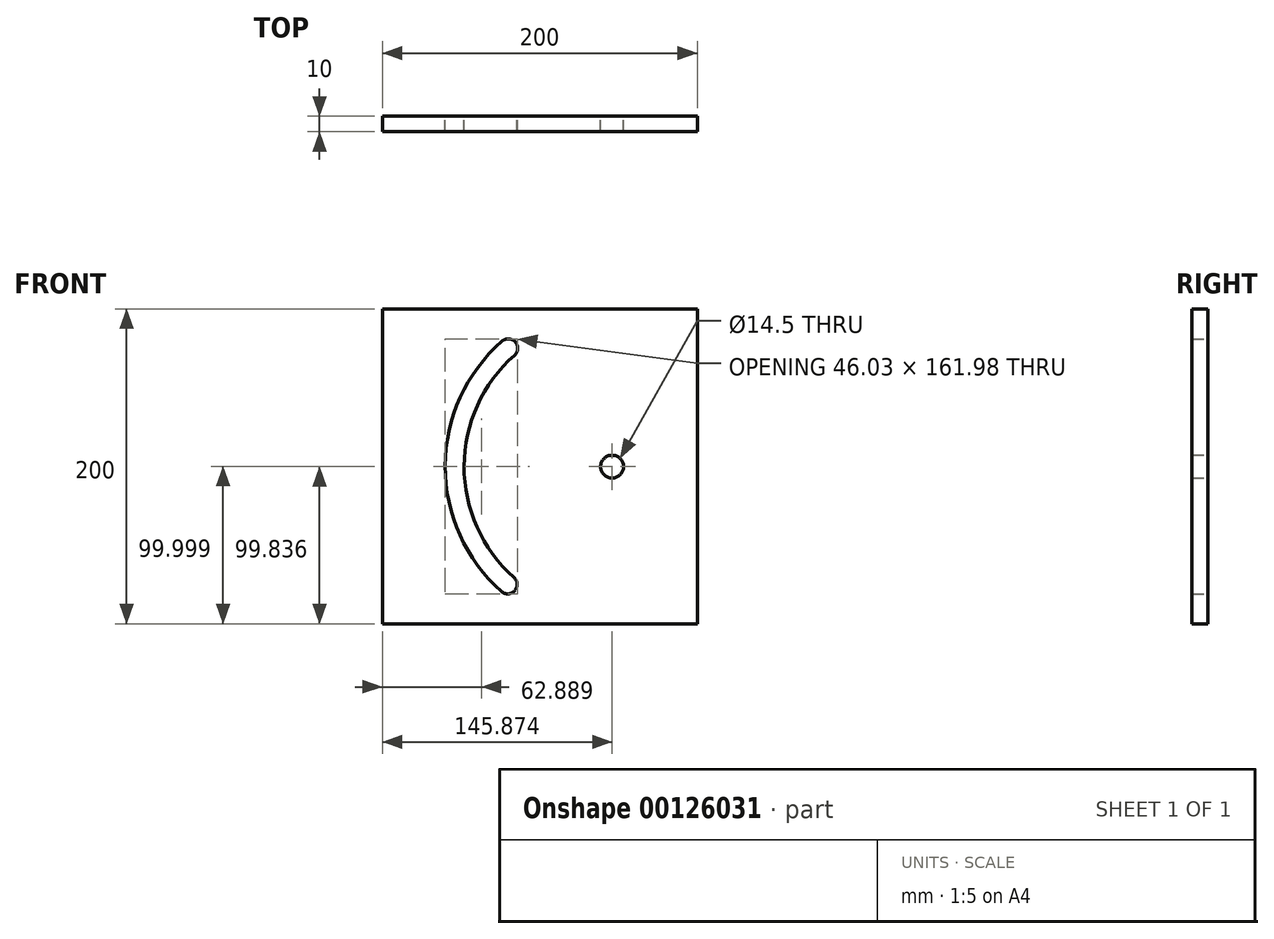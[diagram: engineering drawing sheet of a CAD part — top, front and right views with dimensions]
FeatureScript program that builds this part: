
annotation { "Feature Type Name" : "Feature", "Feature Type Description" : "" }
export const myFeature = defineFeature(function(context is Context, id is Id, definition is map)
    precondition{}
    {
        {
            var Q0;
            Q0=qCreatedBy(makeId("Front.planeOp"),FACE);
            var sketch = newSketch(context, id + "F0", { "sketchPlane" : qUnion([Q0])});
            skLineSegment(sketch, "E0.bottom", {"start": v(100, 100) * mm, "end": v(-100, 100) * mm});
            skLineSegment(sketch, "E0.top", {"start": v(100, -100) * mm, "end": v(-100, -100) * mm});
            skLineSegment(sketch, "E0.left", {"start": v(100, 100) * mm, "end": v(100, -100) * mm});
            skLineSegment(sketch, "E0.right", {"start": v(-100, 100) * mm, "end": v(-100, -100) * mm});
            skPoint(sketch, "E0.middle", {"position": v(0, 0) * mm});
            skArc(sketch, "E1", {"start": v(-20.08, 75) * mm, "mid": v(-54.13, 0.08) * mm, "end": v(-20.46, -75) * mm});
            skArc(sketch, "E2.0.startCap", {"start": v(-24.04, 79.5) * mm, "mid": v(-15.57, 78.96) * mm, "end": v(-16.13, 70.5) * mm});
            skArc(sketch, "E2.0.endCap", {"start": v(-16.48, -70.5) * mm, "mid": v(-15.96, -78.98) * mm, "end": v(-24.43, -79.5) * mm});
            skArc(sketch, "E2.0.left", {"start": v(-16.13, 70.5) * mm, "mid": v(-48.13, 0.07) * mm, "end": v(-16.48, -70.5) * mm});
            skArc(sketch, "E2.0.right", {"start": v(-24.04, 79.5) * mm, "mid": v(-60.13, 0.1) * mm, "end": v(-24.43, -79.5) * mm});
            skCircle(sketch, "E3", {"center": v(45.87, -0.16) * mm, "radius": 7.25 * mm});
            skSolve(sketch);
        }
        {
            var Q0;
            Q0 = qSketchRegion(id + "F0", true);
            extrude(context, id + "F1", {"entities" : qUnion([Q0]), "depth" : 10 * mm});
        }
    });
